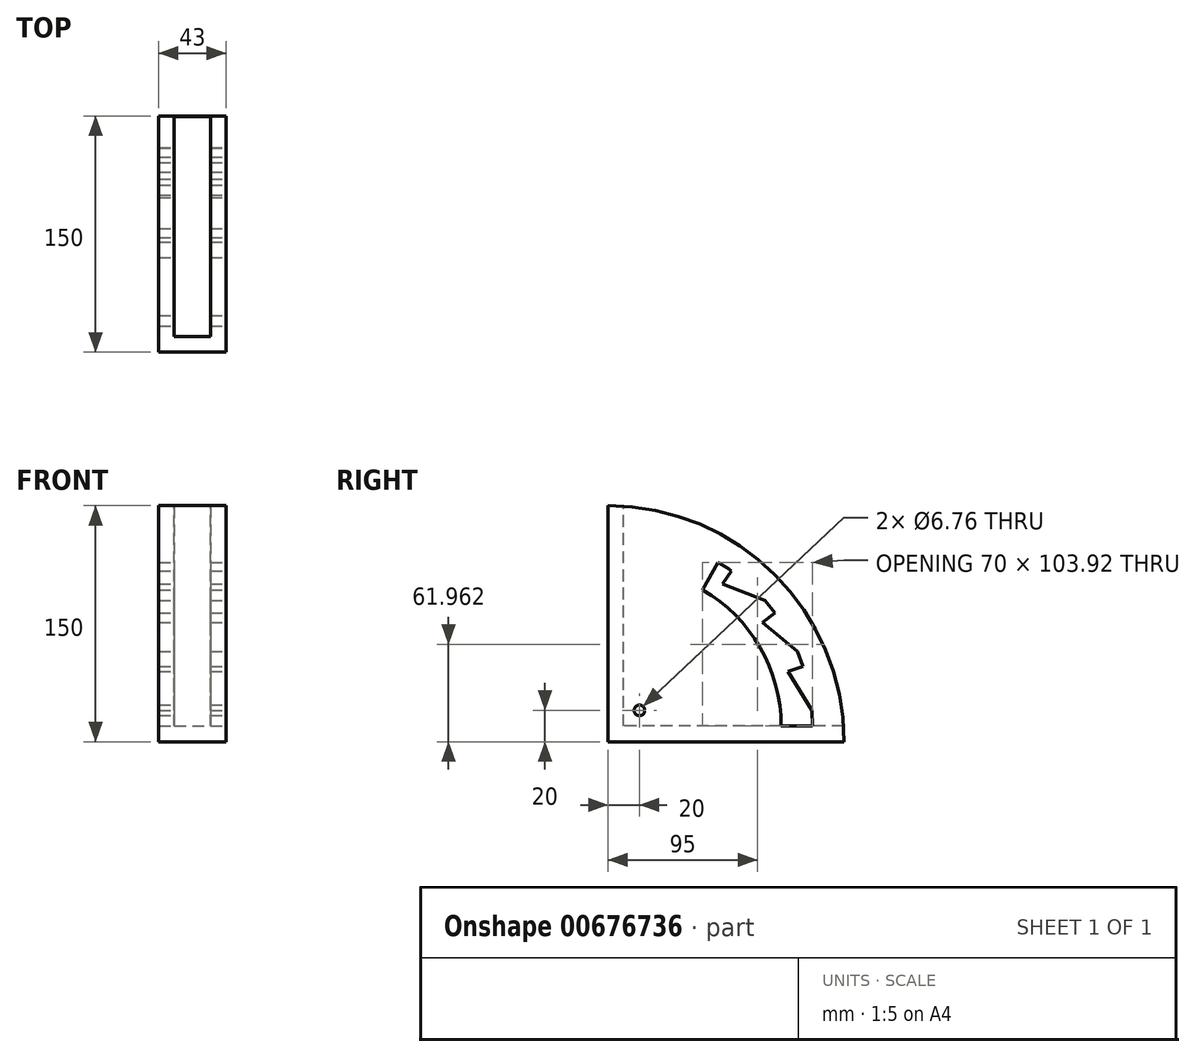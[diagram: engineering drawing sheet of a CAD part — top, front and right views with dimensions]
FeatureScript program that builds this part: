
annotation { "Feature Type Name" : "Feature", "Feature Type Description" : "" }
export const myFeature = defineFeature(function(context is Context, id is Id, definition is map)
    precondition{}
    {
        {
            var Q0;
            Q0=qCreatedBy(makeId("Top.planeOp"),FACE);
            var sketch = newSketch(context, id + "F0", { "sketchPlane" : qUnion([Q0])});
            skLineSegment(sketch, "E0.bottom", {"start": v(21.5, -75) * mm, "end": v(-21.5, -75) * mm});
            skLineSegment(sketch, "E0.top", {"start": v(21.5, 75) * mm, "end": v(-21.5, 75) * mm});
            skLineSegment(sketch, "E0.left", {"start": v(21.5, -75) * mm, "end": v(21.5, 75) * mm});
            skLineSegment(sketch, "E0.right", {"start": v(-21.5, -75) * mm, "end": v(-21.5, 75) * mm});
            skPoint(sketch, "E0.middle", {"position": v(0, 0) * mm});
            skSolve(sketch);
        }
        {
            var Q0;
            Q0 = qSketchRegion(id + "F0", true);
            extrude(context, id + "F1", {"entities" : qUnion([Q0]), "depth" : 150 * mm, "offsetDistance" : 25 * mm});
        }
        {
            var Q0;
            Q0=makeQuery(id+"F1.opExtrude","CAP_FACE",FACE,{"disambiguationData":[OSD([sQuery(id+"F0.wireOp",EDGE,"E0.bottom"),sQuery(id+"F0.wireOp",EDGE,"E0.top"),sQuery(id+"F0.wireOp",EDGE,"E0.left"),sQuery(id+"F0.wireOp",EDGE,"E0.right")])],"isStart":false});
            var sketch = newSketch(context, id + "F2", { "sketchPlane" : qUnion([Q0])});
            skLineSegment(sketch, "E1.bottom", {"start": v(-11.5, 75) * mm, "end": v(11.5, 75) * mm});
            skLineSegment(sketch, "E1.top", {"start": v(-11.5, -65) * mm, "end": v(11.5, -65) * mm});
            skLineSegment(sketch, "E1.left", {"start": v(-11.5, 75) * mm, "end": v(-11.5, -65) * mm});
            skLineSegment(sketch, "E1.right", {"start": v(11.5, 75) * mm, "end": v(11.5, -65) * mm});
            skLineSegment(sketch, "E2", {"start": v(-11.5, -65) * mm, "end": v(-11.5, -75) * mm, "construction": true});
            skLineSegment(sketch, "E3", {"start": v(-11.5, -65) * mm, "end": v(-21.5, -65) * mm, "construction": true});
            skSolve(sketch);
        }
        {
            var Q0;
            Q0 = qSketchRegion(id + "F2", true);
            extrude(context, id + "F3", {"entities" : qUnion([Q0]), "operationType" : NewBodyOperationType.REMOVE, "oppositeDirection" : true, "depth" : 140 * mm, "offsetDistance" : 25 * mm});
        }
        {
            var Q0;
            Q0=makeQuery(id+"F1.opExtrude","SWEPT_FACE",FACE,{"disambiguationData":[OSD([sQuery(id+"F0.wireOp",EDGE,"E0.left")])]});
            var sketch = newSketch(context, id + "F4", { "sketchPlane" : qUnion([Q0])});
            skArc(sketch, "E4", {"start": v(-75, 150) * mm, "mid": v(31.07, 106.07) * mm, "end": v(75, 0) * mm});
            skLineSegment(sketch, "E5", {"start": v(-75, 150) * mm, "end": v(75, 150) * mm});
            skLineSegment(sketch, "E6", {"start": v(75, 150) * mm, "end": v(75, 0) * mm});
            skSolve(sketch);
        }
        {
            var Q0;
            Q0 = qSketchRegion(id + "F4", true);
            extrude(context, id + "F5", {"entities" : qUnion([Q0]), "operationType" : NewBodyOperationType.REMOVE, "endBound" : BoundingType.THROUGH_ALL, "oppositeDirection" : true, "depth" : 25 * mm, "offsetDistance" : 25 * mm});
        }
        {
            var Q0;
            Q0=makeQuery(id+"F1.opExtrude","SWEPT_FACE",FACE,{"disambiguationData":[OSD([sQuery(id+"F0.wireOp",EDGE,"E0.left")])]});
            var sketch = newSketch(context, id + "F6", { "sketchPlane" : qUnion([Q0])});
            skCircle(sketch, "E7", {"center": v(-55, 20) * mm, "radius": 20 * mm});
            skSolve(sketch);
        }
        {
            var Q0;
            Q0=sQuery(id+"F6.wireOp",VERTEX,"E7.center");
            var Q1;
            Q1=makeQuery(id+"F1.opExtrude","SWEPT_BODY",BODY,{"disambiguationData":[OSD([sQuery(id+"F0.wireOp",EDGE,"E0.bottom"),sQuery(id+"F0.wireOp",EDGE,"E0.top"),sQuery(id+"F0.wireOp",EDGE,"E0.left"),sQuery(id+"F0.wireOp",EDGE,"E0.right")])]});
            hole(context, id + "F7", {"style" : HoleStyle.SIMPLE, "endStyle" : HoleEndStyle.THROUGH, "standardTappedOrClearance" : lookupTablePath({ "standard" : "ANSI", "fit" : "Normal (ASME)", "size" : "1/4", "type" : "Clearance" }), "standardBlindInLast" : lookupTablePath({ "fit" : "Free", "standard" : "ANSI", "size" : "1/4", "type" : "Clearance" }), "holeDiameter" : 6.76 * mm, "majorDiameter" : 5 * mm, "isTappedThrough" : true, "tappedDepth" : 12 * mm, "tapClearance" : 3, "locations" : qUnion([Q0]), "scope" : qUnion([Q1])});
        }
        {
            var Q0;
            Q0=makeQuery(id+"F1.opExtrude","SWEPT_FACE",FACE,{"disambiguationData":[OSD([sQuery(id+"F0.wireOp",EDGE,"E0.left")])]});
            var sketch = newSketch(context, id + "F8", { "sketchPlane" : qUnion([Q0])});
            skLineSegment(sketch, "E8", {"start": v(-65, 10) * mm, "end": v(35, 10) * mm, "construction": true});
            skLineSegment(sketch, "E9", {"start": v(-75, 0) * mm, "end": v(-65, 10) * mm, "construction": true});
            skLineSegment(sketch, "E10", {"start": v(-65, 10) * mm, "end": v(-15, 96.6) * mm, "construction": true});
            skLineSegment(sketch, "E11", {"start": v(-15, 96.6) * mm, "end": v(-5, 113.92) * mm});
            skLineSegment(sketch, "E12", {"start": v(35, 10) * mm, "end": v(55, 10) * mm});
            skArc(sketch, "E13", {"start": v(3.44, 108.57) * mm, "mid": v(-0.72, 111.33) * mm, "end": v(-5, 113.92) * mm});
            skLineSegment(sketch, "E14", {"start": v(-2.26, 100.35) * mm, "end": v(3.44, 108.57) * mm});
            skLineSegment(sketch, "E15", {"start": v(-2.26, 100.35) * mm, "end": v(-65, 10) * mm, "construction": true});
            skArc(sketch, "E16", {"start": v(35, 10) * mm, "mid": v(21.6, 60) * mm, "end": v(-15, 96.6) * mm});
            skArc(sketch, "E17", {"start": v(55, 10) * mm, "mid": v(38.92, 70) * mm, "end": v(-5, 113.92) * mm, "construction": true});
            skLineSegment(sketch, "E18", {"start": v(-2.26, 100.35) * mm, "end": v(24.74, 89.66) * mm});
            skLineSegment(sketch, "E19", {"start": v(31.07, 81.91) * mm, "end": v(23.06, 75.92) * mm});
            skLineSegment(sketch, "E20", {"start": v(23.06, 75.92) * mm, "end": v(-65, 10) * mm, "construction": true});
            skLineSegment(sketch, "E21", {"start": v(23.06, 75.92) * mm, "end": v(45.3, 57.25) * mm});
            skLineSegment(sketch, "E22", {"start": v(48.86, 47.9) * mm, "end": v(39.37, 44.74) * mm});
            skLineSegment(sketch, "E23", {"start": v(39.37, 44.74) * mm, "end": v(-65, 10) * mm, "construction": true});
            skLineSegment(sketch, "E24", {"start": v(39.37, 44.74) * mm, "end": v(54.58, 20) * mm});
            skLineSegment(sketch, "E25", {"start": v(24.74, 89.66) * mm, "end": v(31.07, 81.91) * mm});
            skLineSegment(sketch, "E26", {"start": v(45.3, 57.25) * mm, "end": v(48.86, 47.9) * mm});
            skLineSegment(sketch, "E27", {"start": v(54.58, 20) * mm, "end": v(55, 10) * mm});
            skSolve(sketch);
        }
        {
            var Q0;
            Q0 = qSketchRegion(id + "F8", true);
            extrude(context, id + "F9", {"entities" : qUnion([Q0]), "operationType" : NewBodyOperationType.REMOVE, "endBound" : BoundingType.THROUGH_ALL, "oppositeDirection" : true, "depth" : 25 * mm, "offsetDistance" : 25 * mm});
        }
    });
